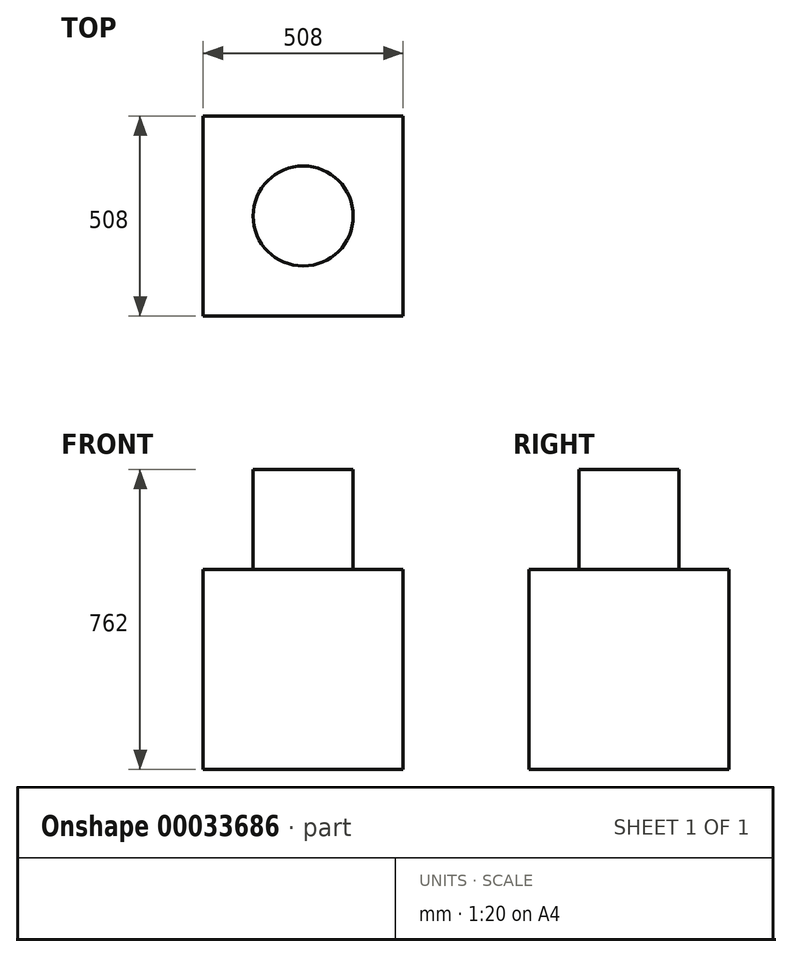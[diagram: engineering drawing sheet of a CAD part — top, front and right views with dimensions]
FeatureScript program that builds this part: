
annotation { "Feature Type Name" : "Feature", "Feature Type Description" : "" }
export const myFeature = defineFeature(function(context is Context, id is Id, definition is map)
    precondition{}
    {
        {
            var Q0;
            Q0=qCreatedBy(makeId("Front.planeOp"),FACE);
            var sketch = newSketch(context, id + "F0", { "sketchPlane" : qUnion([Q0])});
            skLineSegment(sketch, "E0.bottom", {"start": v(-229.89, 317.04) * mm, "end": v(278.11, 317.04) * mm});
            skLineSegment(sketch, "E0.top", {"start": v(-229.89, -190.96) * mm, "end": v(278.11, -190.96) * mm});
            skLineSegment(sketch, "E0.left", {"start": v(-229.89, 317.04) * mm, "end": v(-229.89, -190.96) * mm});
            skLineSegment(sketch, "E0.right", {"start": v(278.11, 317.04) * mm, "end": v(278.11, -190.96) * mm});
            skSolve(sketch);
        }
        {
            var Q0;
            Q0 = qSketchRegion(id + "F0", true);
            extrude(context, id + "F1", {"entities" : qUnion([Q0]), "depth" : 508 * mm});
        }
        {
            var Q0;
            Q0=makeQuery(id+"F1.opExtrude","SWEPT_FACE",FACE,{"disambiguationData":[OSD([sQuery(id+"F0.wireOp",EDGE,"E0.bottom")])]});
            var sketch = newSketch(context, id + "F2", { "sketchPlane" : qUnion([Q0])});
            skCircle(sketch, "E1", {"center": v(24.11, -254) * mm, "radius": 127 * mm});
            skSolve(sketch);
        }
        {
            var Q0;
            Q0 = qSketchRegion(id + "F2", true);
            extrude(context, id + "F3", {"entities" : qUnion([Q0]), "operationType" : NewBodyOperationType.ADD, "depth" : 254 * mm});
        }
    });
